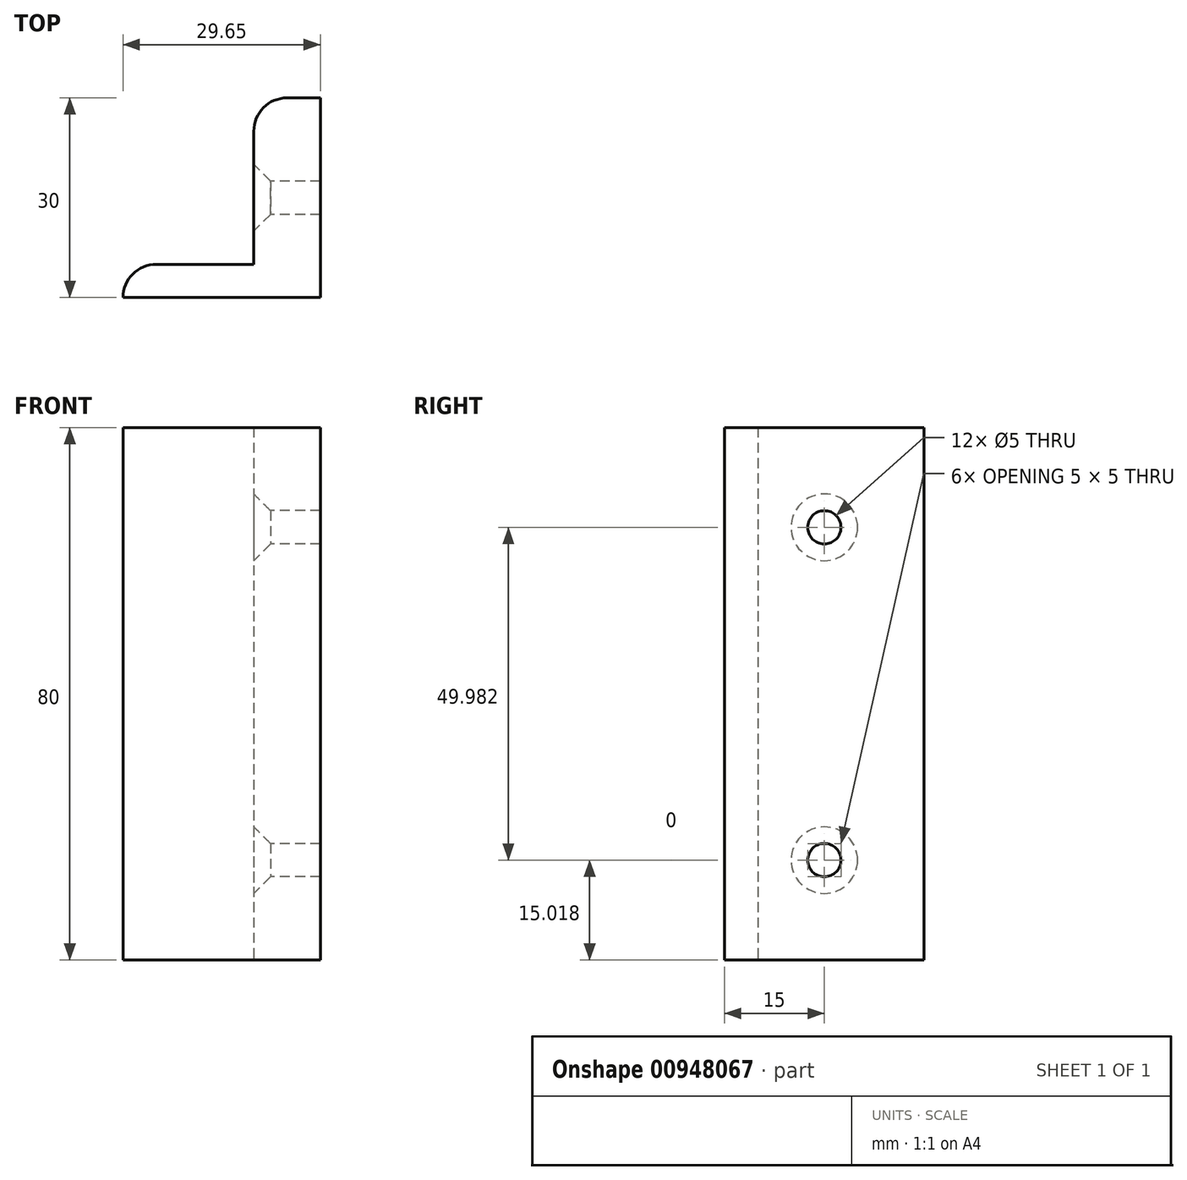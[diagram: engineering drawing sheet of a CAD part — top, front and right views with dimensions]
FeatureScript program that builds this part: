
annotation { "Feature Type Name" : "Feature", "Feature Type Description" : "" }
export const myFeature = defineFeature(function(context is Context, id is Id, definition is map)
    precondition{}
    {
        {
            var Q0;
            Q0=qCreatedBy(makeId("Top.planeOp"),FACE);
            var sketch = newSketch(context, id + "F0", { "sketchPlane" : qUnion([Q0])});
            skLineSegment(sketch, "E0.bottom", {"start": v(10, 30) * mm, "end": v(5, 30) * mm});
            skLineSegment(sketch, "E0.top", {"start": v(10, 0) * mm, "end": v(0, 0) * mm});
            skLineSegment(sketch, "E0.left", {"start": v(10, 30) * mm, "end": v(10, 0) * mm});
            skLineSegment(sketch, "E0.right", {"start": v(0, 25) * mm, "end": v(0, 0) * mm});
            skLineSegment(sketch, "E1.bottom", {"start": v(-14.65, 5) * mm, "end": v(0, 5) * mm});
            skLineSegment(sketch, "E1.top", {"start": v(-19.65, 0) * mm, "end": v(0, 0) * mm});
            skLineSegment(sketch, "E1.left", {"start": v(-19.65, 0) * mm, "end": v(-19.65, 0) * mm});
            skLineSegment(sketch, "E1.right", {"start": v(0, 5) * mm, "end": v(0, 0) * mm});
            skPoint(sketch, "E2.visualSharp", {"position": v(-19.65, 5) * mm});
            skArc(sketch, "E2.filletArc", {"start": v(-14.65, 5) * mm, "mid": v(-18.19, 3.54) * mm, "end": v(-19.65, 0) * mm});
            skPoint(sketch, "E3.visualSharp", {"position": v(0, 30) * mm});
            skArc(sketch, "E3.filletArc", {"start": v(5, 30) * mm, "mid": v(1.46, 28.54) * mm, "end": v(0, 25) * mm});
            skSolve(sketch);
        }
        {
            var Q0;
            Q0=makeQuery(id+"F0.imprint","IMPRINT",FACE,{"disambiguationData":[TD([[makeQuery(id+"F0.imprint","IMPRINT",EDGE,{"derivedFrom":sQuery(id+"F0.wireOp",EDGE,"E0.bottom")}),1.0]])]});
            var Q1;
            Q1=makeQuery(id+"F0.imprint","IMPRINT",FACE,{"disambiguationData":[TD([[makeQuery(id+"F0.imprint","IMPRINT",EDGE,{"derivedFrom":sQuery(id+"F0.wireOp",EDGE,"E1.bottom")}),-1.0]])]});
            extrude(context, id + "F1", {"entities" : qUnion([Q0, Q1]), "depth" : 80 * mm, "offsetDistance" : 25 * mm});
        }
        {
            var Q0;
            Q0=makeQuery(id+"F1.opExtrude","SWEPT_FACE",FACE,{"disambiguationData":[OSD([sQuery(id+"F0.wireOp",EDGE,"E0.right")])]});
            var sketch = newSketch(context, id + "F2", { "sketchPlane" : qUnion([Q0])});
            skPoint(sketch, "E4", {"position": v(-15, 15.02) * mm});
            skPoint(sketch, "E5", {"position": v(-15, 65) * mm});
            skSolve(sketch);
        }
        {
            var Q0;
            Q0=sQuery(id+"F2.wireOp",VERTEX,"E4");
            var Q1;
            Q1=sQuery(id+"F2.wireOp",VERTEX,"E5");
            var Q2;
            Q2=makeQuery(id+"F1.opExtrude","SWEPT_BODY",BODY,{"disambiguationData":[OSD([sQuery(id+"F0.wireOp",EDGE,"E0.bottom"),sQuery(id+"F0.wireOp",EDGE,"E0.top"),sQuery(id+"F0.wireOp",EDGE,"E0.left"),sQuery(id+"F0.wireOp",EDGE,"E0.right"),sQuery(id+"F0.wireOp",EDGE,"E1.bottom"),sQuery(id+"F0.wireOp",EDGE,"E1.top"),sQuery(id+"F0.wireOp",EDGE,"E2.filletArc"),sQuery(id+"F0.wireOp",EDGE,"E3.filletArc")])]});
            hole(context, id + "F3", {"style" : HoleStyle.C_SINK, "endStyle" : HoleEndStyle.THROUGH, "holeDiameter" : 5 * mm, "cSinkDiameter" : 10 * mm, "cSinkAngle" : 90 * degree, "majorDiameter" : 5 * mm, "isTappedThrough" : true, "tappedDepth" : 12 * mm, "tapClearance" : 3, "startFromSketch" : true, "locations" : qUnion([Q0, Q1]), "scope" : qUnion([Q2])});
        }
    });
